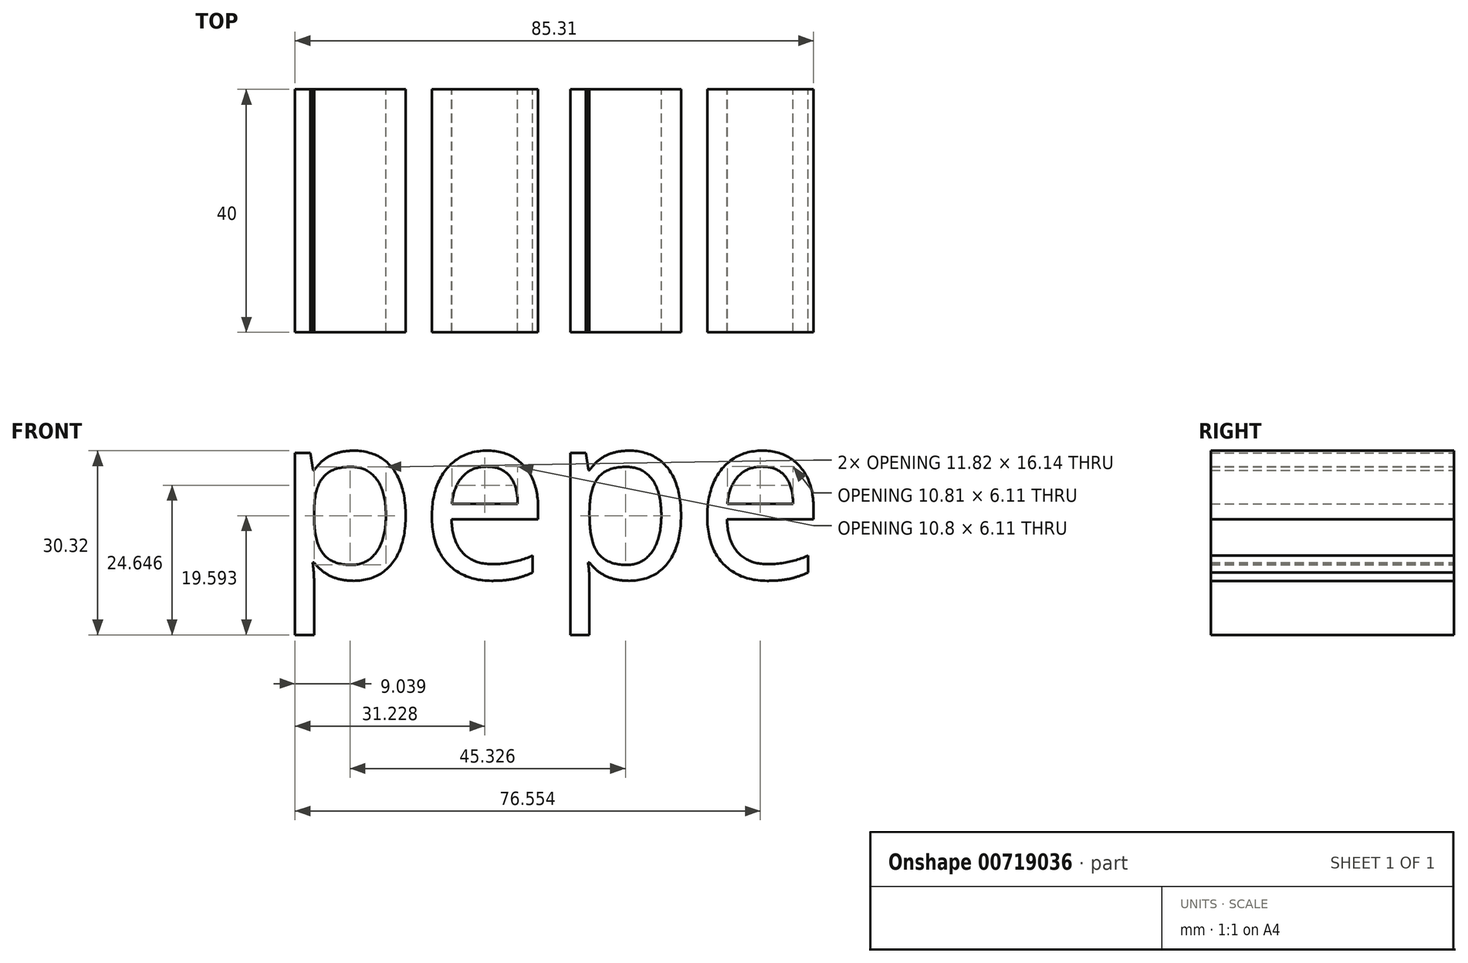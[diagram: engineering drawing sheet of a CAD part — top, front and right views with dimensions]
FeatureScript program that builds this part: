
annotation { "Feature Type Name" : "Feature", "Feature Type Description" : "" }
export const myFeature = defineFeature(function(context is Context, id is Id, definition is map)
    precondition{}
    {
        {
            var Q0;
            Q0=qCreatedBy(makeId("Front.planeOp"),FACE);
            var sketch = newSketch(context, id + "F0", { "sketchPlane" : qUnion([Q0])});
            skText(sketch, "E0", { "text": "pepe", "fontName": "OpenSans-Regular.ttf"});
            const initialGuessF0  = {"E0": [-0.09113, 0.00974, 1, 0, 0.0278]};
            skSetInitialGuess(sketch, initialGuessF0);
            skSolve(sketch);
        }
        {
            var Q0;
            Q0 = qSketchRegion(id + "F0", true);
            extrude(context, id + "F1", {"entities" : qUnion([Q0]), "depth" : 40 * mm, "offsetDistance" : 25 * mm});
        }
    });
